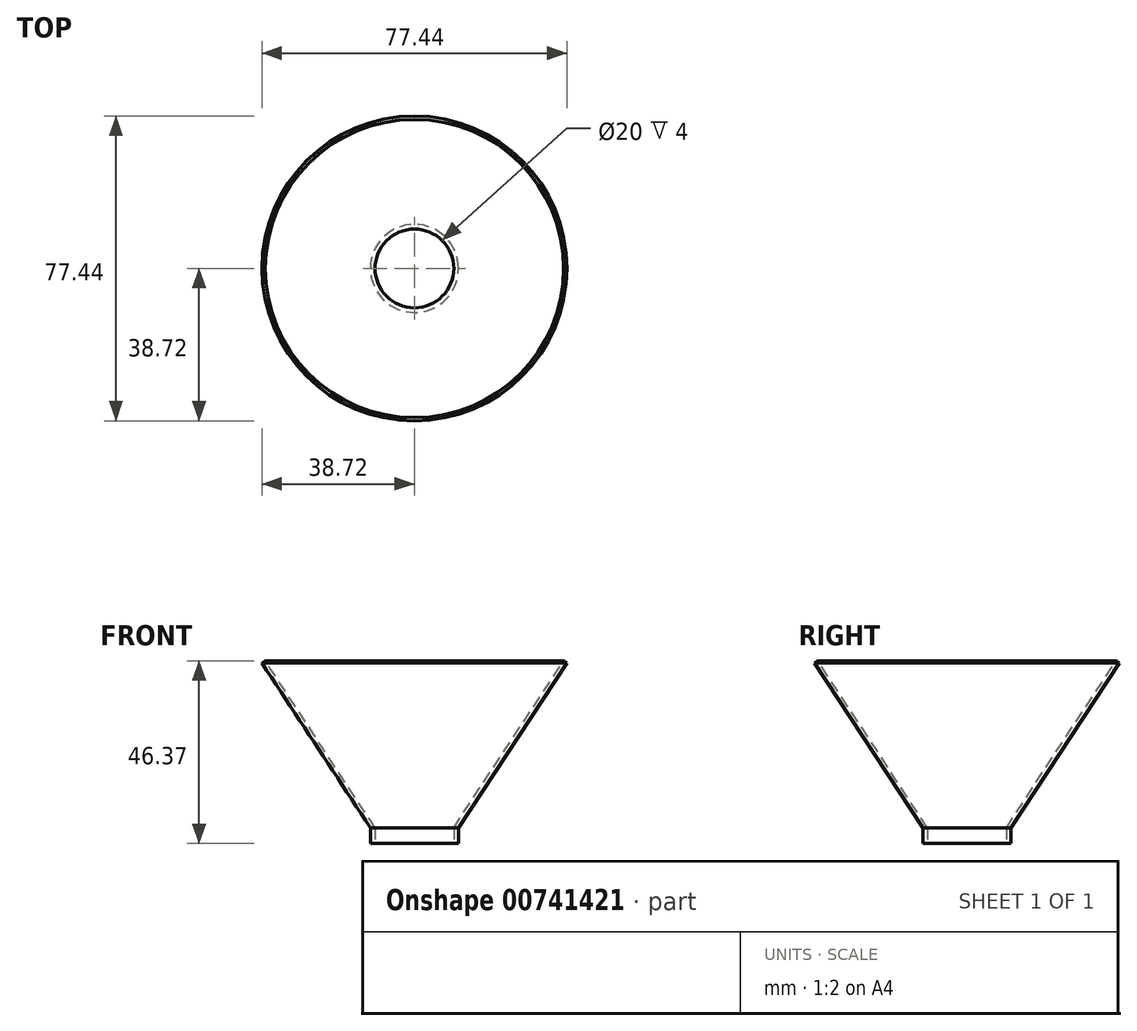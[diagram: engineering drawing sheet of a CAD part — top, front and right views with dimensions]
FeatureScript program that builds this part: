
annotation { "Feature Type Name" : "Feature", "Feature Type Description" : "" }
export const myFeature = defineFeature(function(context is Context, id is Id, definition is map)
    precondition{}
    {
        {
            var Q0;
            Q0=qCreatedBy(makeId("Front.planeOp"),FACE);
            var sketch = newSketch(context, id + "F0", { "sketchPlane" : qUnion([Q0])});
            skLineSegment(sketch, "E0", {"start": v(0, 0) * mm, "end": v(-10, 0) * mm});
            skLineSegment(sketch, "E1", {"start": v(-10, 0) * mm, "end": v(-10, 4) * mm});
            skLineSegment(sketch, "E2", {"start": v(-10, 4) * mm, "end": v(-37.88, 46.37) * mm});
            skLineSegment(sketch, "E3", {"start": v(-37.88, 46.37) * mm, "end": v(-38.72, 45.82) * mm});
            skLineSegment(sketch, "E4", {"start": v(-38.72, 45.82) * mm, "end": v(-11.2, 4) * mm});
            skLineSegment(sketch, "E5", {"start": v(-11.2, 4) * mm, "end": v(-11.2, 0) * mm});
            skLineSegment(sketch, "E6", {"start": v(-11.2, 0) * mm, "end": v(-10, 0) * mm});
            skLineSegment(sketch, "E7", {"start": v(0, 0) * mm, "end": v(0, 7.47) * mm});
            skSolve(sketch);
        }
        {
            var Q0;
            Q0=makeQuery(id+"F0.imprint","IMPRINT",FACE,{"disambiguationData":[TD([[makeQuery(id+"F0.imprint","IMPRINT",EDGE,{"derivedFrom":sQuery(id+"F0.wireOp",EDGE,"E1")}),1.0]])]});
            var Q1;
            Q1=sQuery(id+"F0.wireOp",EDGE,"E7");
            revolve(context, id + "F1", {"surfaceOperationType" : NewSurfaceOperationType.NEW, "entities" : qUnion([Q0]), "axis" : qUnion([Q1]), "revolveType" : RevolveType.FULL});
        }
    });
